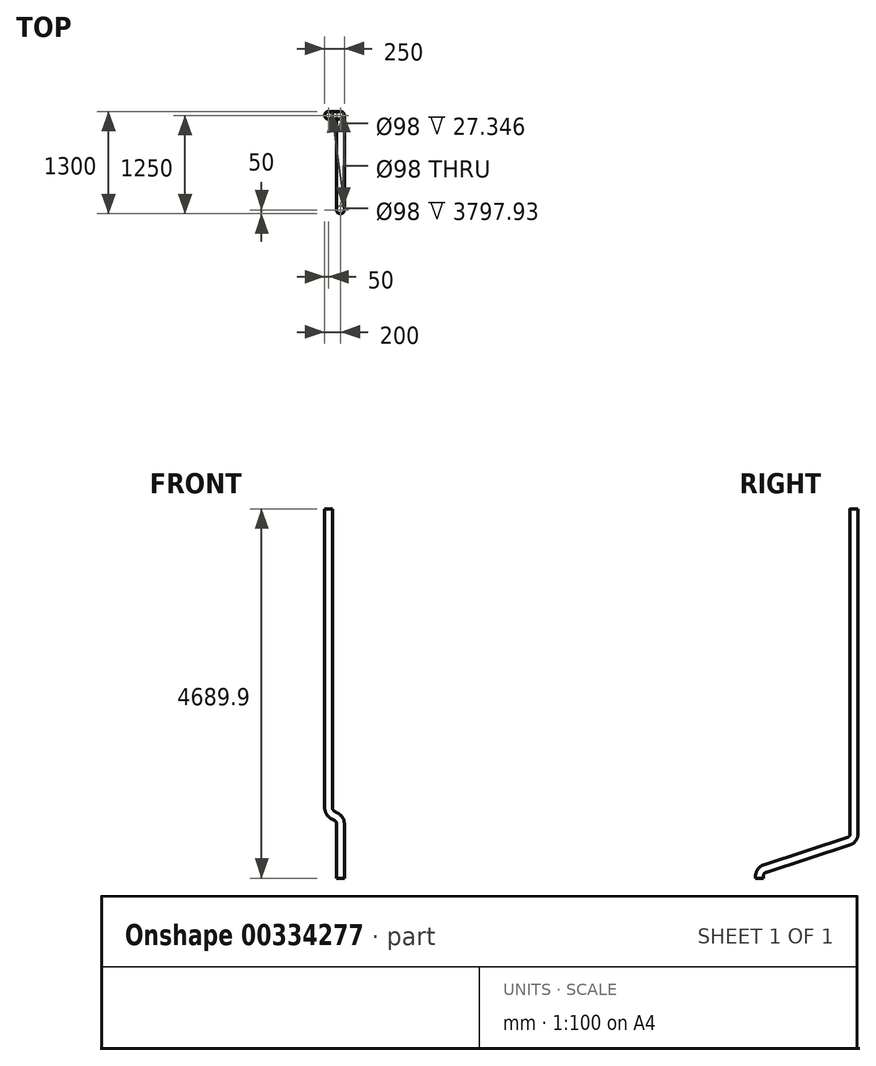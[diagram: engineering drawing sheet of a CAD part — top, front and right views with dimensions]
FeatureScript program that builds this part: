
annotation { "Feature Type Name" : "Feature", "Feature Type Description" : "" }
export const myFeature = defineFeature(function(context is Context, id is Id, definition is map)
    precondition{}
    {
        {
            var Q0;
            Q0=qCreatedBy(makeId("Right.planeOp"),FACE);
            var sketch = newSketch(context, id + "F0", { "sketchPlane" : qUnion([Q0])});
            skLineSegment(sketch, "E0", {"start": v(0, 0) * mm, "end": v(0, -27.35) * mm});
            skLineSegment(sketch, "E1", {"start": v(-69.1, -122.45) * mm, "end": v(-1130.9, -467.45) * mm});
            skLineSegment(sketch, "E2", {"start": v(-1200, -562.56) * mm, "end": v(-1200, -589.9) * mm});
            skPoint(sketch, "E3.visualSharp", {"position": v(0, -100) * mm});
            skArc(sketch, "E3.filletArc", {"start": v(-69.1, -122.45) * mm, "mid": v(-19.1, -86.12) * mm, "end": v(0, -27.35) * mm});
            skPoint(sketch, "E4.visualSharp", {"position": v(-1200, -489.9) * mm});
            skArc(sketch, "E4.filletArc", {"start": v(-1130.9, -467.45) * mm, "mid": v(-1180.9, -503.78) * mm, "end": v(-1200, -562.56) * mm});
            skSolve(sketch);
        }
        {
            var Q0;
            Q0=qCreatedBy(makeId("Top.planeOp"),FACE);
            var sketch = newSketch(context, id + "F1", { "sketchPlane" : qUnion([Q0])});
            skCircle(sketch, "E5", {"center": v(0, 0) * mm, "radius": 50 * mm});
            skCircle(sketch, "E6", {"center": v(0, 0) * mm, "radius": 49 * mm});
            skSolve(sketch);
        }
        {
            var Q0;
            Q0=makeQuery(id+"F1.imprint","IMPRINT",FACE,{"disambiguationData":[TD([[makeQuery(id+"F1.imprint","IMPRINT",EDGE,{"derivedFrom":sQuery(id+"F1.wireOp",EDGE,"E5")}),1.0]])]});
            var Q1;
            Q1=sQuery(id+"F0.wireOp",EDGE,"E0");
            var Q2;
            Q2=sQuery(id+"F0.wireOp",EDGE,"E3.filletArc");
            var Q3;
            Q3=sQuery(id+"F0.wireOp",EDGE,"E1");
            var Q4;
            Q4=sQuery(id+"F0.wireOp",EDGE,"E4.filletArc");
            var Q5;
            Q5=sQuery(id+"F0.wireOp",EDGE,"E2");
            sweep(context, id + "F2", {"profiles" : qUnion([Q0]), "path" : qUnion([Q1, Q2, Q3, Q4, Q5])});
        }
        {
            var Q0;
            Q0=qCreatedBy(makeId("Front.planeOp"),FACE);
            var sketch = newSketch(context, id + "F3", { "sketchPlane" : qUnion([Q0])});
            skLineSegment(sketch, "E7", {"start": v(0, 0) * mm, "end": v(0, 100) * mm});
            skLineSegment(sketch, "E8", {"start": v(-50, 186.6) * mm, "end": v(-100, 215.47) * mm});
            skLineSegment(sketch, "E9", {"start": v(-150, 302.07) * mm, "end": v(-150, 4100) * mm});
            skPoint(sketch, "E10.visualSharp", {"position": v(0, 157.74) * mm});
            skArc(sketch, "E10.filletArc", {"start": v(0, 100) * mm, "mid": v(-13.4, 150) * mm, "end": v(-50, 186.6) * mm});
            skPoint(sketch, "E11.visualSharp", {"position": v(-150, 244.34) * mm});
            skArc(sketch, "E11.filletArc", {"start": v(-150, 302.07) * mm, "mid": v(-136.6, 252.07) * mm, "end": v(-100, 215.47) * mm});
            skSolve(sketch);
        }
        {
            var Q0;
            Q0=makeQuery(id+"F2.opSweep","CAP_FACE",FACE,{"disambiguationData":[OSD([sQuery(id+"F0.wireOp",VERTEX,"E0.start"),sQuery(id+"F1.wireOp",EDGE,"E5"),sQuery(id+"F1.wireOp",EDGE,"E6")])],"isStart":true});
            var Q1;
            Q1=sQuery(id+"F3.wireOp",EDGE,"E7");
            var Q2;
            Q2=sQuery(id+"F3.wireOp",EDGE,"E10.filletArc");
            var Q3;
            Q3=sQuery(id+"F3.wireOp",EDGE,"E8");
            var Q4;
            Q4=sQuery(id+"F3.wireOp",EDGE,"E11.filletArc");
            var Q5;
            Q5=sQuery(id+"F3.wireOp",EDGE,"E9");
            sweep(context, id + "F4", {"operationType" : NewBodyOperationType.ADD, "profiles" : qUnion([Q0]), "path" : qUnion([Q1, Q2, Q3, Q4, Q5])});
        }
    });
